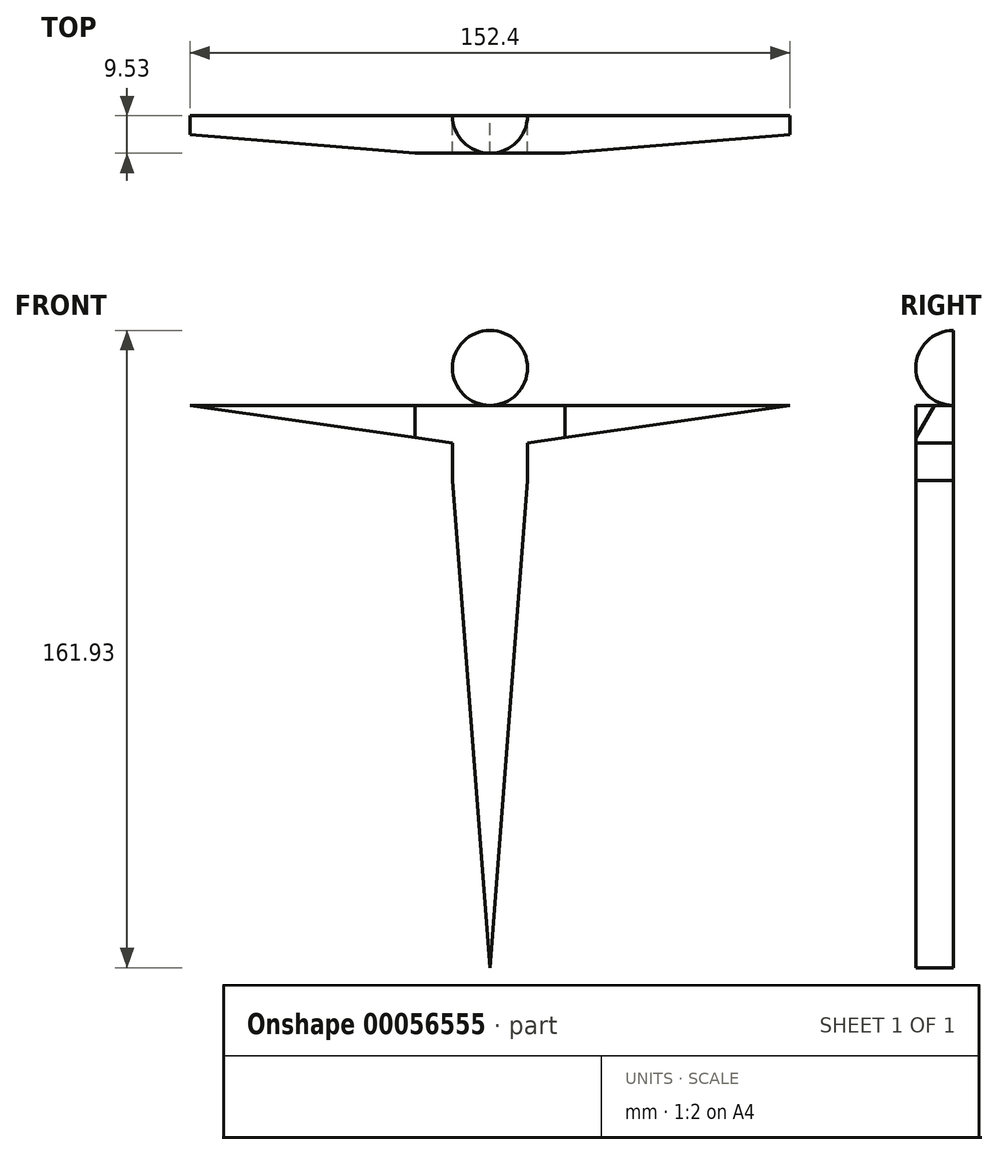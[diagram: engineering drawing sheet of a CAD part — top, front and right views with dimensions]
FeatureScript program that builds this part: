
annotation { "Feature Type Name" : "Feature", "Feature Type Description" : "" }
export const myFeature = defineFeature(function(context is Context, id is Id, definition is map)
    precondition{}
    {
        {
            var Q0;
            Q0=qCreatedBy(makeId("Front.planeOp"),FACE);
            var sketch = newSketch(context, id + "F0", { "sketchPlane" : qUnion([Q0])});
            skLineSegment(sketch, "E0.rect.bottom", {"start": v(-9.53, -19.05) * mm, "end": v(9.53, -19.05) * mm});
            skLineSegment(sketch, "E0.rect.top", {"start": v(-9.53, 0) * mm, "end": v(9.53, 0) * mm});
            skLineSegment(sketch, "E0.rect.left", {"start": v(-9.53, -19.05) * mm, "end": v(-9.53, 0) * mm});
            skLineSegment(sketch, "E0.rect.right", {"start": v(9.53, -19.05) * mm, "end": v(9.53, 0) * mm});
            skPoint(sketch, "E0.rect.middle", {"position": v(0, -9.53) * mm});
            skCircle(sketch, "E1", {"center": v(0, 9.53) * mm, "radius": 9.53 * mm});
            skLineSegment(sketch, "E2", {"start": v(9.52, 0) * mm, "end": v(76.2, 0) * mm});
            skLineSegment(sketch, "E3", {"start": v(9.52, -9.53) * mm, "end": v(76.2, 0) * mm});
            skLineSegment(sketch, "E4", {"start": v(9.53, -19.05) * mm, "end": v(0, -142.88) * mm});
            skLineSegment(sketch, "E5", {"start": v(0, -19.05) * mm, "end": v(0, -142.88) * mm});
            skLineSegment(sketch, "E6.MirrorCS", {"start": v(-9.53, -19.05) * mm, "end": v(0, -142.88) * mm});
            skLineSegment(sketch, "E7.MirrorCS", {"start": v(-9.53, 0) * mm, "end": v(-76.2, 0) * mm});
            skLineSegment(sketch, "E8.MirrorCS", {"start": v(-9.52, -9.53) * mm, "end": v(-76.2, 0) * mm});
            skLineSegment(sketch, "E9", {"start": v(0, 65.83) * mm, "end": v(0, -100.94) * mm, "construction": true});
            skLineSegment(sketch, "E10", {"start": v(-82.52, 0) * mm, "end": v(-82.52, 0) * mm});
            skPoint(sketch, "E10.endSnap0", {"position": v(42.86, 0) * mm});
            skLineSegment(sketch, "E11", {"start": v(0, 19.05) * mm, "end": v(0, 0) * mm});
            skSolve(sketch);
        }
        {
            var Q0;
            {var subQ6=sQuery(id+"F0.wireOp",EDGE,"E0.rect.bottom");var subQ8=makeQuery(id+"F0.imprint","INTERSECT",VERTEX,{"derivedFrom":[subQ6,sQuery(id+"F0.wireOp",EDGE,"E5")]});Q0=makeQuery(id+"F0.imprint","IMPRINT",FACE,{"disambiguationData":[TD([[makeQuery(id+"F0.imprint","IMPRINT",EDGE,{"disambiguationData":[TD([[subQ8,1.0]])],"derivedFrom":subQ6}),1.0]])]});}
            var Q1;
            {var subQ0=sQuery(id+"F0.wireOp",EDGE,"E7.MirrorCS");Q1=makeQuery(id+"F0.imprint","IMPRINT",FACE,{"disambiguationData":[TD([[makeQuery(id+"F0.imprint","IMPRINT",EDGE,{"derivedFrom":subQ0}),1.0]])]});}
            var Q2;
            {var subQ0=sQuery(id+"F0.wireOp",EDGE,"E2");Q2=makeQuery(id+"F0.imprint","IMPRINT",FACE,{"disambiguationData":[TD([[makeQuery(id+"F0.imprint","IMPRINT",EDGE,{"derivedFrom":subQ0}),-1.0]])]});}
            var Q3;
            {var subQ2=sQuery(id+"F0.wireOp",EDGE,"E5");Q3=makeQuery(id+"F0.imprint","IMPRINT",FACE,{"disambiguationData":[TD([[makeQuery(id+"F0.imprint","IMPRINT",EDGE,{"derivedFrom":subQ2}),-1.0]])]});}
            var Q4;
            {var subQ0=sQuery(id+"F0.wireOp",EDGE,"E4");Q4=makeQuery(id+"F0.imprint","IMPRINT",FACE,{"disambiguationData":[TD([[makeQuery(id+"F0.imprint","IMPRINT",EDGE,{"derivedFrom":subQ0}),-1.0]])]});}
            extrude(context, id + "F1", {"entities" : qUnion([Q0, Q1, Q2, Q3, Q4]), "depth" : 9.52 * mm});
        }
        {
            var Q0;
            {var subQ0=sQuery(id+"F0.wireOp",EDGE,"E11");Q0=makeQuery(id+"F0.imprint","IMPRINT",FACE,{"disambiguationData":[TD([[makeQuery(id+"F0.imprint","IMPRINT",EDGE,{"derivedFrom":subQ0}),-1.0]])]});}
            var Q1;
            Q1=sQuery(id+"F0.wireOp",EDGE,"E9");
            revolve(context, id + "F2", {"entities" : qUnion([Q0]), "axis" : qUnion([Q1]), "revolveType" : RevolveType.ONE_DIRECTION, "oppositeDirection" : true, "angle" : 180 * degree});
        }
        {
            var Q0;
            Q0=makeQuery(id+"F1.opExtrude","SWEPT_FACE",FACE,{"disambiguationData":[OSD([sQuery(id+"F0.wireOp",EDGE,"E0.rect.top"),sQuery(id+"F0.wireOp",EDGE,"E2"),sQuery(id+"F0.wireOp",EDGE,"E7.MirrorCS")])]});
            var sketch = newSketch(context, id + "F3", { "sketchPlane" : qUnion([Q0])});
            skLineSegment(sketch, "E12", {"start": v(-76.2, -9.53) * mm, "end": v(-76.2, -4.76) * mm});
            skLineSegment(sketch, "E13", {"start": v(-76.2, -4.76) * mm, "end": v(-19.05, -9.53) * mm});
            skLineSegment(sketch, "E14.MirrorCS", {"start": v(76.2, -4.76) * mm, "end": v(19.05, -9.53) * mm});
            skLineSegment(sketch, "E15.MirrorCS", {"start": v(76.2, -9.53) * mm, "end": v(76.2, -4.76) * mm});
            skSolve(sketch);
        }
        {
            var Q0;
            Q0 = qSketchRegion(id + "F3", true);
            var Q1;
            {var subQ0=sQuery(id+"F3.wireOp",EDGE,"E12");Q1=makeQuery(id+"F3.imprint","IMPRINT",FACE,{"disambiguationData":[TD([[makeQuery(id+"F3.imprint","IMPRINT",EDGE,{"derivedFrom":subQ0}),-1.0]])]});}
            var Q2;
            {var subQ0=sQuery(id+"F3.wireOp",EDGE,"E14.MirrorCS");Q2=makeQuery(id+"F3.imprint","IMPRINT",FACE,{"disambiguationData":[TD([[makeQuery(id+"F3.imprint","IMPRINT",EDGE,{"derivedFrom":subQ0}),1.0]])]});}
            extrude(context, id + "F4", {"entities" : qUnion([Q0, Q1, Q2]), "operationType" : NewBodyOperationType.REMOVE, "endBound" : BoundingType.THROUGH_ALL, "oppositeDirection" : true, "depth" : 25.4 * mm});
        }
    });
